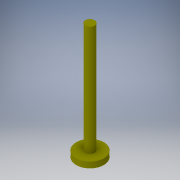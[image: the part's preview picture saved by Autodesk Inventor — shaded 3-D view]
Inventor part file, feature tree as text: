
AUTODESK INVENTOR PART (.ipt)
format: ipt  version: 2019 (Build 230136000, 136)  size: 111,616 bytes
history: native  units: mm
features: extrude x2, sketch x2
ambient origin geometry x8: Origin, YZ Plane, XZ Plane, XY Plane, X Axis, Y Axis, Z Axis, Center Point
bodies: Solid1 (feature_tree)
feature tree (4):
  extrude  "Extrusion1"  Depth=60.0mm TaperAngle=0.0deg
  extrude  "Extrusion2"  Depth=3.18mm TaperAngle=0.0deg
  sketch  "Sketch1"  dims[d0=5.0mm d1=60.0mm d2=0.0mm]
  sketch  "Sketch2"  dims[d3=15.0mm d4=3.18mm d5=0.0mm]
